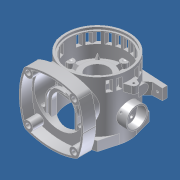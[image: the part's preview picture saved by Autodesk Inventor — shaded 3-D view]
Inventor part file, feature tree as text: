
AUTODESK INVENTOR PART (.ipt)
format: ipt  version: unknown  size: 1,210,880 bytes
history: native  units: in
note: dims shown in document units (in); Inventor stores cm internally (conversion verified against a paired STEP export)
features: extrude x28, sketch x24, plane x15, projected_geometry x10, loft x4, fillet x3, mirror x1, revolve x1, pattern_circular x1, chamfer x1
ambient origin geometry x8: Origin, YZ Plane, XZ Plane, XY Plane, X Axis, Y Axis, Z Axis, Center Point
bodies: Solid1 (feature_tree)
feature tree (88):
  extrude  "Extrusion1"  Depth=2.425in
  extrude  "Extrusion2"  Depth=0.1625in
  plane  "Work Plane3"
  sketch  "Sketch4"  dims[d8=0.1in d9=0.1in]
  plane  "Work Plane4"
  extrude  "Extrusion3"  Depth=0.1in
  sketch  "Sketch6"  dims[d17=0.575in d18=0.0in d19=2.625in]
  extrude  "Extrusion6"  Depth=0.1in
  extrude  "Extrusion7"  Depth=2.625in
  sketch  "Sketch8"  dims[d25=0.1in d27=0.25in]
  extrude  "Extrusion8"  Depth=3.15in
  extrude  "Extrusion10"  Depth=0.25in
  plane  "Work Plane5"
  sketch  "Sketch9"  dims[d29=0.1625in d30=-0.05in]
  extrude  "Extrusion12"  [1 undecoded]
  extrude  "Extrusion13"  Depth=0.1in
  plane  "Work Plane6"
  extrude  "Extrusion15"  Depth=2.725in TaperAngle=0.0deg
  extrude  "Extrusion16"  Depth=2.725in TaperAngle=0.0deg
  plane  "Work Plane7"
  plane  "Work Plane8"
  plane  "Work Plane9"
  sketch  "Sketch15"  dims[d50=1.7in d51=0.25in]
  sketch  "Sketch13"  dims[d42=0.1in d43=2.725in d44=0.0in]
  extrude  "Extrusion19"  [1 undecoded]
  extrude  "Extrusion20"  Depth=0.25in
  plane  "Work Plane11"
  sketch  "Sketch14"  dims[d47=2.725in d48=0.0in d49=-0.125in]
  extrude  "Extrusion21"  Depth=0.0625in
  plane  "Work Plane12"
  extrude  "Extrusion22"  Depth=0.175in
  mirror  "Mirror3"
  extrude  "Extrusion23"  Depth=4.0in
  plane  "Work Plane15"
  sketch  "Sketch20"  dims[d61=0.1in d62=0.0in d65=4.0in]
  plane  "Work Plane16"
  plane  "Work Plane17"
  extrude  "Extrusion30"  Depth=0.575in
  extrude  "Extrusion25"  Depth=2.001in
  extrude  "Extrusion26"  Depth=0.375in
  extrude  "Extrusion27"  Depth=0.25in TaperAngle=0.0deg
  extrude  "Extrusion29"  Depth=0.55in
  extrude  "Extrusion31"  Depth=1.5748in
  extrude  "Extrusion32"  Depth=0.2375in
  plane  "Work Plane18"
  extrude  "Extrusion33"  Depth=0.7874in
  plane  "Work Plane19"
  revolve  "Revolution1"  [1 undecoded]
  pattern_circular  "Circular Pattern1"  [2 undecoded]
  extrude  "Extrusion34"  Depth=0.2375in
  extrude  "Extrusion36"  Depth=0.2375in
  sketch  "Sketch29"  dims[d87=0.175in d95=1.5748in d97=0.3625in d98=0.3937in d100=1.0in]
  plane  "Work Plane20"
  sketch  "Sketch30"  dims[d102=1.5748in d104=0.3625in d105=0.3937in d107=1.0in d111=0.2375in]
  loft  "Loft1"
  loft  "Loft2"
  loft  "Loft3"
  loft  "Loft4"
  extrude  "Extrusion37"  Depth=1.25in
  extrude  "Extrusion38"  Depth=0.25in TaperAngle=0.0deg
  fillet  "Fillet1"  Radius=0.25in
  fillet  "Fillet3"  [1 undecoded]
  fillet  "Fillet4"  Radius=0.375in
  chamfer  "Chamfer1"  Distance=0.125in
  sketch  "Sketch1"  dims[d0=0.25in d1=2.425in]
  sketch  "Sketch2"  dims[d4=2.425in d5=0.1625in]
  projected_geometry  "Projected Loop1"
  projected_geometry  "Projected Loop2"
  sketch  "Sketch5"  dims[d10=0.1in d11=0.1in]
  sketch  "Sketch7"  dims[d20=0.1in d21=0.0in d24=3.15in]
  projected_geometry  "Projected Loop3"
  projected_geometry  "Projected Loop4"
  sketch  "Sketch11"  dims[d31=0.1in d32=0.0in d35=0.1in]
  sketch  "Sketch12"  dims[d38=0.5in d39=0.0in d40=2.725in d41=0.0in]
  sketch  "Sketch16"  dims[d52=0.25in d55=0.0625in]
  sketch  "Sketch18"  dims[d58=2.725in d59=0.0in d60=0.175in]
  projected_geometry  "Projected Loop6"
  sketch  "Sketch23"  dims[d66=0.75in d67=0.575in]
  sketch  "Sketch24"  dims[d69=1.185in d71=2.001in]
  projected_geometry  "Projected Loop8"
  sketch  "Sketch25"  dims[d72=0.25in d73=0.0in d81=0.375in]
  projected_geometry  "Projected Loop9"
  projected_geometry  "Projected Loop10"
  sketch  "Sketch26"  dims[d82=0.0in d83=0.25in d84=0.0in]
  sketch  "Sketch28"  dims[d85=0.2375in d86=0.55in]
  projected_geometry  "Projected Loop12"
  sketch  "Sketch31"  dims[d112=0.7in d113=0.7874in d115=0.3625in d116=0.3937in d118=1.0in d120=0.675in d121=0.125in d122=0.2375in d123=0.2375in d124=3.05in d127=0.4125in d128=1.0in d129=1.1375in d130=1.25in d131=0.25in d132=0.0in d133=0.25in d134=0.0in d136=-0.5in d139=0.375in d140=0.125in d141=0.375in d142=0.0in d143=1.9175in d147=-0.125in d148=0.635in d149=0.5in d151=0.325in d152=0.375in d153=0.0in d154=0.375in d155=0.0in d156=1.1811in d158=360.0deg d160=0.175in d161=0.275in d167=-1.835in d168=0.1in d169=0.0in d170=1.125in d172=0.25in d173=0.175in d174=0.375in d175=0.175in d177=0.4125in d178=0.0in d179=45.0deg d180=0.175in d181=0.1875in d182=0.0875in d183=0.25in d184=0.0in d185=90.0deg d189=90.0deg d190=0.25in d191=0.175in d192=1.0in d193=0.0in d194=0.075in d195=1.265in d196=0.0in d197=1.265in d198=0.0in d199=1.265in d200=0.0in d201=90.0deg d202=0.175in d203=0.25in d204=1.265in d205=0.0in d206=90.0deg d208=0.175in d209=0.025in d210=90.0deg d211=1.5748in d212=360.0deg d214=0.0625in d216=0.375in d217=1.265in d218=0.0in d221=1.265in d222=0.0in d223=0.0312in d224=0.0312in d225=0.125in d226=0.125in d227=90.0deg d228=2.45in d229=-0.05in d230=0.225in d231=1.5748in d233=360.0deg d235=0.0in d236=90.0deg d237=0.0in d238=90.0deg d239=0.0in d240=90.0deg d241=0.0in d242=90.0deg d243=0.0in d244=90.0deg d245=0.0in d246=90.0deg d247=0.0in d248=90.0deg d249=0.0in d250=90.0deg d251=0.375in d252=0.0in d253=0.125in d254=0.0156in d255=0.125in d256=1.265in d257=0.0in d258=0.025in d259=0.125in d260=45.0deg d263=0.5in d265=3.375in]
  projected_geometry  "Projected Loop13"
note: 6 required parameter values undecoded (feature->parameter linkage not recoverable at this tier; creation-order binding heuristic only, values carry confidence <= 0.55)